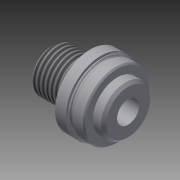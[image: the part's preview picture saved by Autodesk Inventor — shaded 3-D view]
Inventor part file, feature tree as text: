
AUTODESK INVENTOR PART (.ipt)
format: ipt  version: 2014 SP2 (Build 180246200, 246)  size: 217,088 bytes
history: native  units: in
note: dims shown in document units (in); Inventor stores cm internally (conversion verified against a paired STEP export)
features: other x84, sketch x5, revolve x4, thread x1, hole x1
ambient origin geometry x8: Origin, YZ Plane, XZ Plane, XY Plane, X Axis, Y Axis, Z Axis, Center Point
bodies: Solid1 (feature_tree)
feature tree (95):
  revolve  "Revolution1"  [1 undecoded]
  thread  "Thread1"  [1 undecoded]
  revolve  "Revolution2"  Angle=360.0deg
  revolve  "Revolution3"  [1 undecoded]
  hole  "Hole1"  [1 undecoded]
  revolve  "Revolution4"  [1 undecoded]
  other  "hh_XY"
  other  "hh_YZ"
  other  "hh_ZX"
  other  "hh_X"
  other  "hh_Y"
  other  "hh_Z"
  other  "hh_Center"
  other  "rod_guide_XY"
  other  "rod_guide_YZ"
  other  "rod_guide_ZX"
  other  "rod_guide_X"
  other  "rod_guide_Y"
  other  "rod_guide_Z"
  other  "rod_guide_Center"
  other  "t1_XY"
  other  "t1_YZ"
  other  "t1_ZX"
  other  "t1_X"
  other  "t1_Y"
  other  "t1_Z"
  other  "t1_Center"
  other  "t111_XY"
  other  "t111_YZ"
  other  "t111_ZX"
  other  "t111_X"
  other  "t111_Y"
  other  "t111_Z"
  other  "t111_Center"
  other  "to_foot_bracket_XY"
  other  "to_foot_bracket_YZ"
  other  "to_foot_bracket_ZX"
  other  "to_foot_bracket_X"
  other  "to_foot_bracket_Y"
  other  "to_foot_bracket_Z"
  other  "to_foot_bracket_Center"
  other  "to_nut_XY"
  other  "to_nut_YZ"
  other  "to_nut_ZX"
  other  "to_nut_X"
  other  "to_nut_Y"
  other  "to_nut_Z"
  other  "to_nut_Center"
  other  "to_rod_XY"
  other  "to_rod_YZ"
  other  "to_rod_ZX"
  other  "to_rod_X"
  other  "to_rod_Y"
  other  "to_rod_Z"
  other  "to_rod_Center"
  other  "to_screw_XY"
  other  "to_screw_YZ"
  other  "to_screw_ZX"
  other  "to_screw_X"
  other  "to_screw_Y"
  other  "to_screw_Z"
  other  "to_screw_Center"
  other  "to_trunnion_brackets_XY"
  other  "to_trunnion_brackets_YZ"
  other  "to_trunnion_brackets_ZX"
  other  "to_trunnion_brackets_X"
  other  "to_trunnion_brackets_Y"
  other  "to_trunnion_brackets_Z"
  other  "to_trunnion_brackets_Center"
  other  "to_trunnion_brackets1_XY"
  other  "to_trunnion_brackets1_YZ"
  other  "to_trunnion_brackets1_ZX"
  other  "to_trunnion_brackets1_X"
  other  "to_trunnion_brackets1_Y"
  other  "to_trunnion_brackets1_Z"
  other  "to_trunnion_brackets1_Center"
  other  "to_trunnion_brackets2_XY"
  other  "to_trunnion_brackets2_YZ"
  other  "to_trunnion_brackets2_ZX"
  other  "to_trunnion_brackets2_X"
  other  "to_trunnion_brackets2_Y"
  other  "to_trunnion_brackets2_Z"
  other  "to_trunnion_brackets2_Center"
  other  "to_tube_XY"
  other  "to_tube_YZ"
  other  "to_tube_ZX"
  other  "to_tube_X"
  other  "to_tube_Y"
  other  "to_tube_Z"
  other  "to_tube_Center"
  sketch  "Sketch_1"  dims[d0=360.0deg d1=0.4083in d2=0.0in d3=360.0deg]
  sketch  "Sketch_3"  dims[d4=360.0deg]
  sketch  "Sketch_4"  dims[d5=0.2535in d6=0.75in d7=0.2735in d8=0.25in d9=90.0deg d10=0.875in d11=0.0in d12=360.0deg]
  sketch  "Sketch4"  dims[d13=0.0in d14=0.0in d15=0.0in d16=0.0in d17=0.0in d18=0.0in]
  sketch  "Sketch_47"
note: 5 required parameter values undecoded (feature->parameter linkage not recoverable at this tier; creation-order binding heuristic only, values carry confidence <= 0.55)